# Revit family: AFX-Crain-Outdoor_Sconce
name_source: partatom
category: Lighting Fixtures
units: mm (PartAtom-declared; Revit-internal decimal feet)

## family parameters
Cut with Voids When Loaded = No
Host = Face
Light Source = Yes
Maintain Annotation Orientation = No
Part Type = Normal
Room Calculation Point = No
Round Connector Dimension = Use Diameter
Shared = No

## types (2) — shared parameters
Apparent Load = 0 VA
Assembly Code = D5020200
Color Filter = 16777215
Default Elevation = 48"
Depth = 6"
Diffuser Finish = AFX - Diffuser
Dimming Lamp Color Temperature Shift = <None>
Emit Shape Visible in Rendering = No
Emit from Circle Diameter = 5"
Frame Finish = AFX - Paint Black
Keynote = 12500
Manufacturer = AFX Inc
Power Factor = 1
Product Documentation Link = https://www.afxinc.com
Revit Model Built By = https://www.servex-us.com
Tilt Angle = 90.00°
Type Comments = Crain
URL = https://www.afxinc.com
Voltage = 120 V
Width = 5 1/2"

## per-type parameters (varying)
| type | Description | Height | Photometric Web File | Wattage Comments |
| CRNW0616 | LED Outdoor Sconce - 5 1/2"W x 6"D x 16"H | 16" | CRNW0616LAJUDBK_3000K_IES.IES | 20W |
| CRNW0624 | LED Outdoor Sconce - 5 1/2"W x 6"D x 24"H | 24" | CRNW0624LAJUDTG_3000K_IES.IES | 24W |

note: column(s) folded — value = type name in every type: Model

## geometry (parser evidence)
native form markers: Sweep x2
no freeform markers — native parametric forms only
